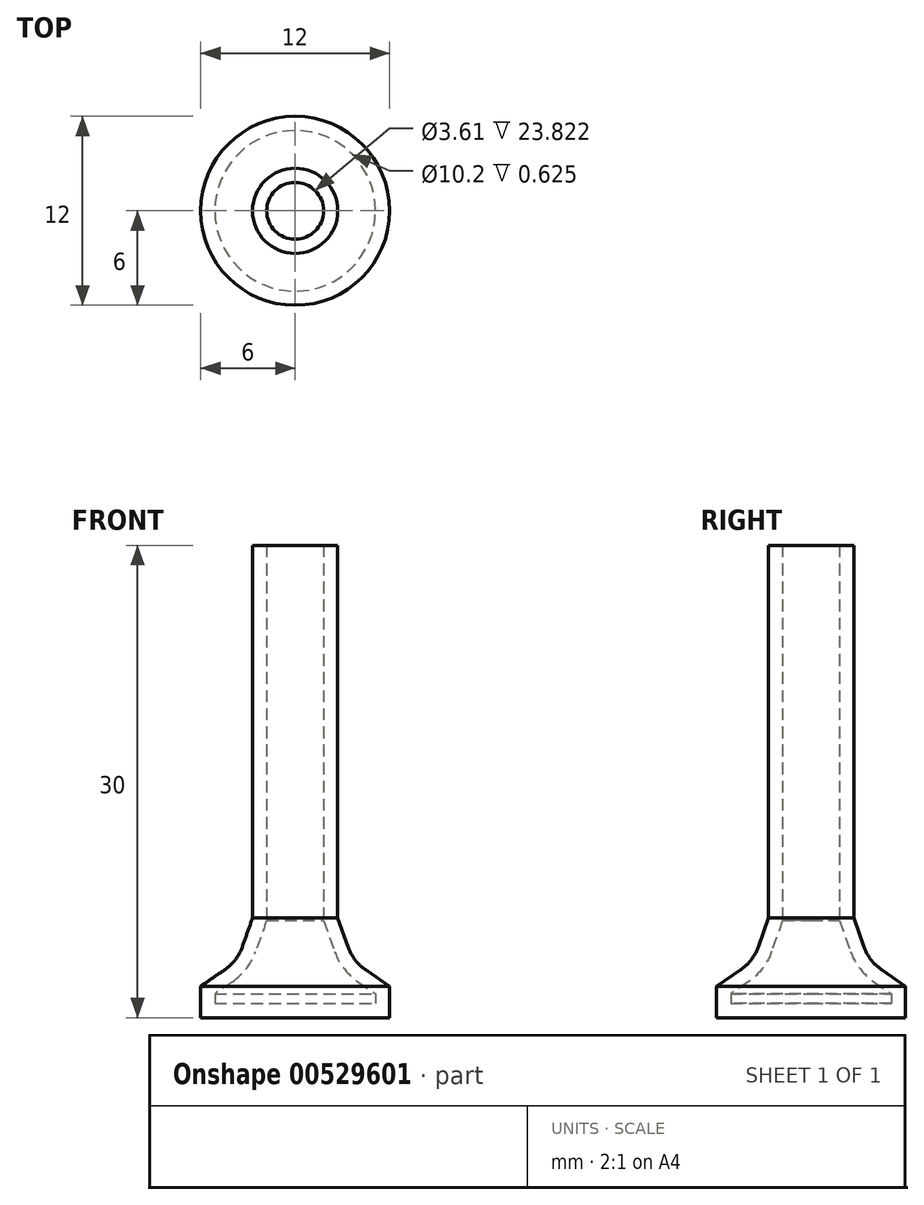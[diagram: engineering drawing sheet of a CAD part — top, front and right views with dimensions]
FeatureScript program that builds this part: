
annotation { "Feature Type Name" : "Feature", "Feature Type Description" : "" }
export const myFeature = defineFeature(function(context is Context, id is Id, definition is map)
    precondition{}
    {
        {
            var Q0;
            Q0=qCreatedBy(makeId("Front.planeOp"),FACE);
            var sketch = newSketch(context, id + "F0", { "sketchPlane" : qUnion([Q0])});
            skLineSegment(sketch, "E0", {"start": v(0, 0) * mm, "end": v(0, 30) * mm});
            skLineSegment(sketch, "E1", {"start": v(0, 30) * mm, "end": v(-2.7, 30) * mm});
            skLineSegment(sketch, "E2", {"start": v(-2.7, 30) * mm, "end": v(-2.7, 6.33) * mm});
            skLineSegment(sketch, "E3", {"start": v(0, 0) * mm, "end": v(-6, 0) * mm});
            skLineSegment(sketch, "E4", {"start": v(-2.7, 6.33) * mm, "end": v(-3.35, 4.5) * mm});
            skLineSegment(sketch, "E5", {"start": v(-6, 0) * mm, "end": v(-6, 2) * mm});
            skLineSegment(sketch, "E6", {"start": v(-6, 2) * mm, "end": v(-4.49, 3.03) * mm});
            skPoint(sketch, "E7.visualSharp", {"position": v(-3.68, 3.58) * mm});
            skArc(sketch, "E7.filletArc", {"start": v(-4.49, 3.03) * mm, "mid": v(-3.8, 3.68) * mm, "end": v(-3.35, 4.5) * mm});
            skSolve(sketch);
        }
        {
            var Q0;
            Q0=makeQuery(id+"F0.imprint","IMPRINT",FACE,{"disambiguationData":[TD([[makeQuery(id+"F0.imprint","IMPRINT",EDGE,{"derivedFrom":sQuery(id+"F0.wireOp",EDGE,"E0")}),1.0]])]});
            var Q1;
            Q1=sQuery(id+"F0.wireOp",EDGE,"E0");
            revolve(context, id + "F1", {"entities" : qUnion([Q0]), "axis" : qUnion([Q1]), "revolveType" : RevolveType.FULL});
        }
        {
            var Q0;
            Q0=makeQuery(id+"F1.opRevolve","SWEPT_FACE",FACE,{"disambiguationData":[OSD([sQuery(id+"F0.wireOp",EDGE,"E1")])]});
            shell(context, id + "F2", {"entities" : qUnion([Q0]), "thickness" : 0.9 * mm});
        }
    });
